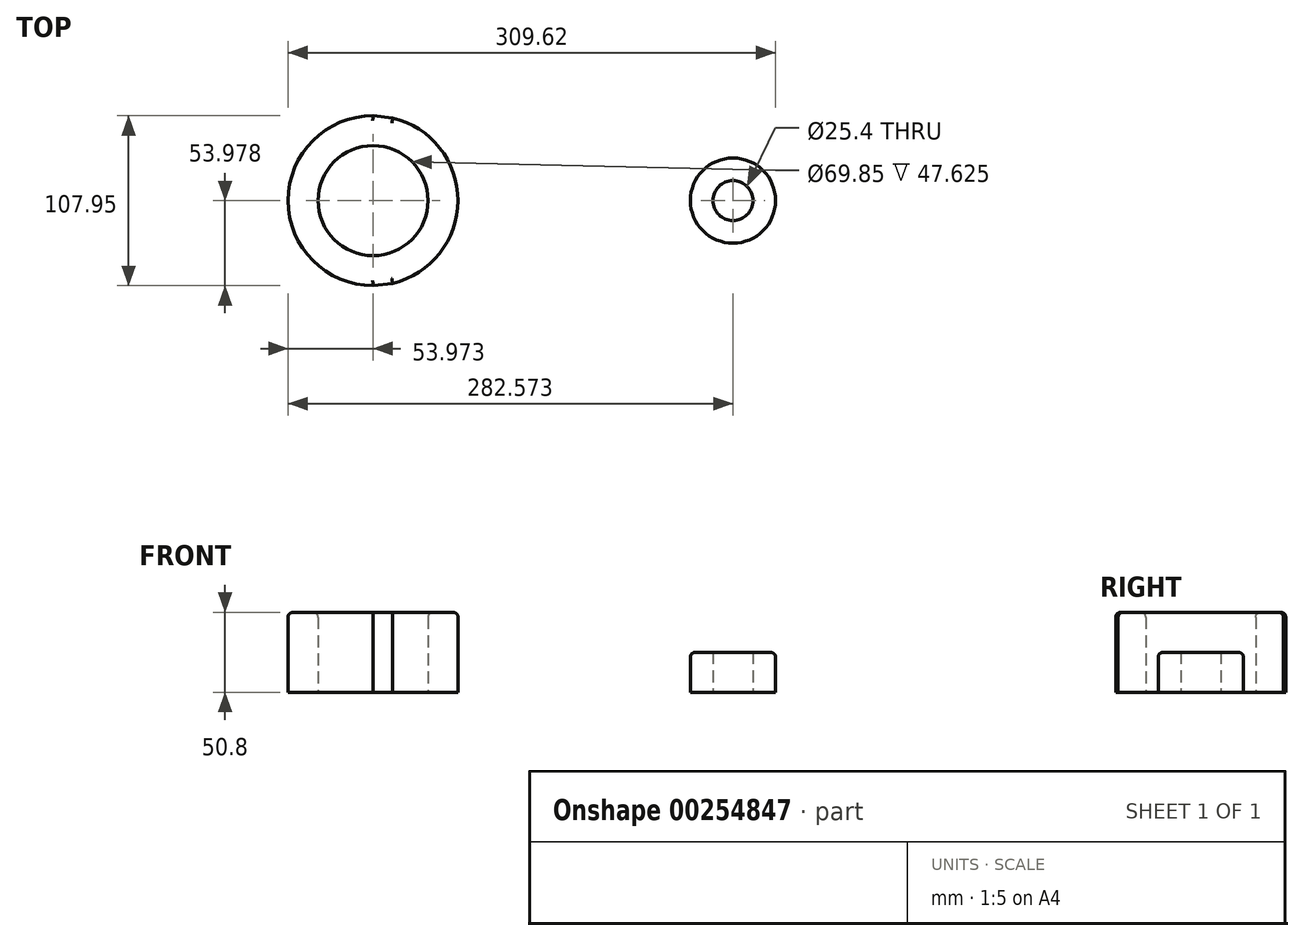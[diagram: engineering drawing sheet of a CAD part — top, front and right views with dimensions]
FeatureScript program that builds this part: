
annotation { "Feature Type Name" : "Feature", "Feature Type Description" : "" }
export const myFeature = defineFeature(function(context is Context, id is Id, definition is map)
    precondition{}
    {
        {
            var Q0;
            Q0=qCreatedBy(makeId("Top.planeOp"),FACE);
            var sketch = newSketch(context, id + "F0", { "sketchPlane" : qUnion([Q0])});
            skCircle(sketch, "E0", {"center": v(-125.2, 22.72) * mm, "radius": 53.98 * mm});
            skCircle(sketch, "E1", {"center": v(103.4, 22.72) * mm, "radius": 27.05 * mm});
            skCircle(sketch, "E2", {"center": v(103.4, 22.72) * mm, "radius": 12.7 * mm});
            skCircle(sketch, "E3", {"center": v(-125.2, 22.72) * mm, "radius": 34.93 * mm});
            skLineSegment(sketch, "E4", {"start": v(-125.2, 76.7) * mm, "end": v(103.4, 49.77) * mm});
            skLineSegment(sketch, "E5", {"start": v(-125.2, -31.26) * mm, "end": v(103.4, -4.52) * mm});
            skArc(sketch, "E6", {"start": v(-49, 38.6) * mm, "mid": v(-64.87, 22.72) * mm, "end": v(-49, 6.84) * mm});
            skArc(sketch, "E7", {"start": v(39.9, 6.84) * mm, "mid": v(55.78, 22.72) * mm, "end": v(39.9, 38.6) * mm});
            skLineSegment(sketch, "E8", {"start": v(-49, 38.6) * mm, "end": v(39.9, 38.6) * mm});
            skLineSegment(sketch, "E9", {"start": v(-49, 6.84) * mm, "end": v(39.9, 6.84) * mm});
            skSolve(sketch);
        }
        {
            var Q0;
            {var subQ0=sQuery(id+"F0.wireOp",EDGE,"E4");var subQ1=sQuery(id+"F0.wireOp",EDGE,"E0");var subQ2=makeQuery(id+"F0.imprint","INTERSECT",VERTEX,{"disambiguationData":[OD(0.0)],"derivedFrom":[subQ1,subQ0]});Q0=makeQuery(id+"F0.imprint","IMPRINT",FACE,{"disambiguationData":[TD([[makeQuery(id+"F0.imprint","IMPRINT",EDGE,{"disambiguationData":[TD([[subQ2,1.0]])],"derivedFrom":subQ1}),1.0]])]});}
            var Q1;
            {var subQ0=sQuery(id+"F0.wireOp",EDGE,"E5");var subQ1=sQuery(id+"F0.wireOp",EDGE,"E0");var subQ2=makeQuery(id+"F0.imprint","INTERSECT",VERTEX,{"disambiguationData":[OD(0.0)],"derivedFrom":[subQ1,subQ0]});Q1=makeQuery(id+"F0.imprint","IMPRINT",FACE,{"disambiguationData":[TD([[makeQuery(id+"F0.imprint","IMPRINT",EDGE,{"disambiguationData":[TD([[subQ2,-1.0]])],"derivedFrom":subQ1}),1.0]])]});}
            var Q2;
            Q2=makeQuery(id+"F0.imprint","IMPRINT",FACE,{"disambiguationData":[TD([[makeQuery(id+"F0.imprint","IMPRINT",EDGE,{"derivedFrom":sQuery(id+"F0.wireOp",EDGE,"E3")}),-1.0]])]});
            extrude(context, id + "F1", {"entities" : qUnion([Q0, Q1, Q2]), "depth" : 50.8 * mm});
        }
        {
            var Q0;
            Q0=makeQuery(id+"F0.imprint","IMPRINT",FACE,{"disambiguationData":[TD([[makeQuery(id+"F0.imprint","IMPRINT",EDGE,{"derivedFrom":sQuery(id+"F0.wireOp",EDGE,"E1")}),1.0]])]});
            extrude(context, id + "F2", {"entities" : qUnion([Q0]), "depth" : 25.4 * mm});
        }
        {
            var Q0;
            Q0=makeQuery(id+"F1.opExtrude","CAP_FACE",FACE,{"disambiguationData":[OSD([sQuery(id+"F0.wireOp",EDGE,"E0"),sQuery(id+"F0.wireOp",EDGE,"E3")])],"isStart":false});
            fillet(context, id + "F3", {"entities" : qUnion([Q0]), "radius" : 3.17 * mm, "tangentPropagation" : true, "allowEdgeOverflow" : false});
        }
        {
            var Q0;
            Q0=makeQuery(id+"F2.opExtrude","CAP_EDGE",EDGE,{"disambiguationData":[OSD([sQuery(id+"F0.wireOp",EDGE,"E1")])],"isStart":false});
            fillet(context, id + "F4", {"entities" : qUnion([Q0]), "radius" : 3.17 * mm, "tangentPropagation" : true, "allowEdgeOverflow" : false});
        }
    });
